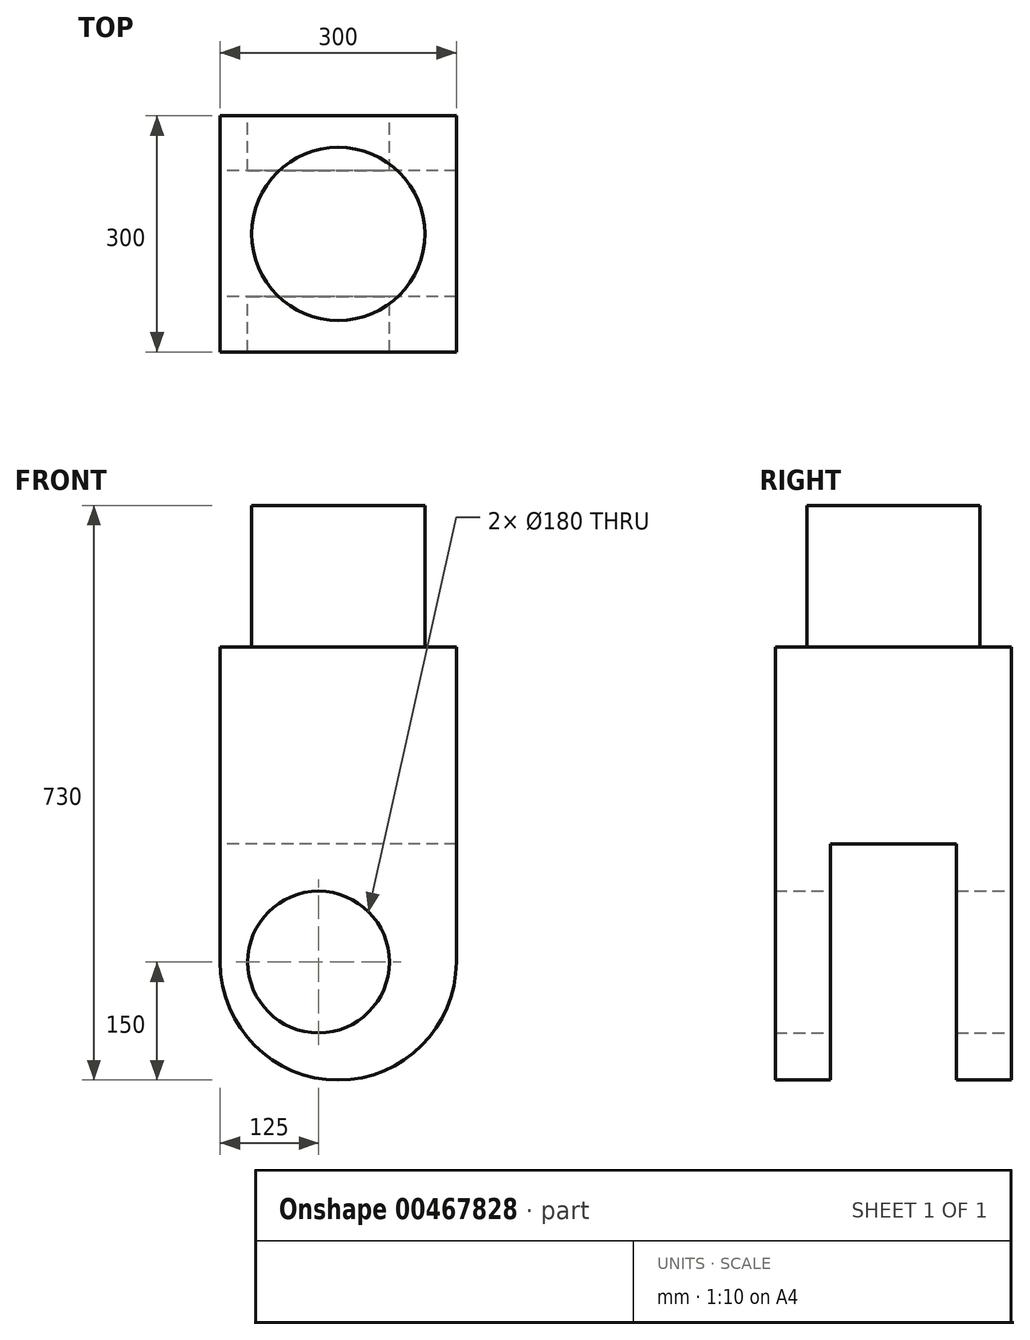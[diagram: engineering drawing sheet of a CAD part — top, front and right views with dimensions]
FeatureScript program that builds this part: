
annotation { "Feature Type Name" : "Feature", "Feature Type Description" : "" }
export const myFeature = defineFeature(function(context is Context, id is Id, definition is map)
    precondition{}
    {
        {
            var Q0;
            Q0=qCreatedBy(makeId("Top.planeOp"),FACE);
            var sketch = newSketch(context, id + "F0", { "sketchPlane" : qUnion([Q0])});
            skCircle(sketch, "E0", {"center": v(0, 0) * mm, "radius": 90 * mm});
            skSolve(sketch);
        }
        {
            var Q0;
            Q0 = qSketchRegion(id + "F0", true);
            extrude(context, id + "F1", {"entities" : qUnion([Q0]), "depth" : 180 * mm});
        }
        {
            var Q0;
            Q0=makeQuery(id+"F1.opExtrude","CAP_FACE",FACE,{"disambiguationData":[OSD([sQuery(id+"F0.wireOp",EDGE,"E0")])],"isStart":true});
            var sketch = newSketch(context, id + "F2", { "sketchPlane" : qUnion([Q0])});
            skLineSegment(sketch, "E1.bottom", {"start": v(150, 150) * mm, "end": v(-150, 150) * mm});
            skLineSegment(sketch, "E1.top", {"start": v(150, -150) * mm, "end": v(-150, -150) * mm});
            skLineSegment(sketch, "E1.left", {"start": v(150, 150) * mm, "end": v(150, -150) * mm});
            skLineSegment(sketch, "E1.right", {"start": v(-150, 150) * mm, "end": v(-150, -150) * mm});
            skPoint(sketch, "E1.middle", {"position": v(0, 0) * mm});
            skSolve(sketch);
        }
        {
            var Q0;
            Q0 = qSketchRegion(id + "F2", true);
            extrude(context, id + "F3", {"entities" : qUnion([Q0]), "operationType" : NewBodyOperationType.ADD, "depth" : 400 * mm, "offsetDistance" : 25 * mm});
        }
        {
            var Q0;
            Q0=makeQuery(id+"F3.opExtrude","SWEPT_FACE",FACE,{"disambiguationData":[OSD([sQuery(id+"F2.wireOp",EDGE,"E1.top")])]});
            var sketch = newSketch(context, id + "F4", { "sketchPlane" : qUnion([Q0])});
            skArc(sketch, "E2", {"start": v(-150, -400) * mm, "mid": v(0, -550) * mm, "end": v(150, -400) * mm});
            skLineSegment(sketch, "E3", {"start": v(150, -400) * mm, "end": v(-150, -400) * mm});
            skSolve(sketch);
        }
        {
            var Q0;
            Q0 = qSketchRegion(id + "F4", true);
            extrude(context, id + "F5", {"entities" : qUnion([Q0]), "operationType" : NewBodyOperationType.ADD, "oppositeDirection" : true, "depth" : 300 * mm});
        }
        {
            var Q0;
            Q0=makeQuery(id+"F5.boolean.opBoolean","MERGE",FACE,{"derivedFrom":[makeQuery(id+"F3.opExtrude","SWEPT_FACE",FACE,{"disambiguationData":[OSD([sQuery(id+"F2.wireOp",EDGE,"E1.top")])]}),makeQuery(id+"F5.opExtrude","CAP_FACE",FACE,{"disambiguationData":[OSD([sQuery(id+"F4.wireOp",EDGE,"E2"),sQuery(id+"F4.wireOp",EDGE,"E3")])],"isStart":true})]});
            var sketch = newSketch(context, id + "F6", { "sketchPlane" : qUnion([Q0])});
            skCircle(sketch, "E4", {"center": v(25, -400) * mm, "radius": 90 * mm});
            skSolve(sketch);
        }
        {
            var Q0;
            Q0 = qSketchRegion(id + "F6", true);
            extrude(context, id + "F7", {"entities" : qUnion([Q0]), "operationType" : NewBodyOperationType.REMOVE, "oppositeDirection" : true, "depth" : 300 * mm});
        }
        {
            var Q0;
            Q0=makeQuery(id+"F3.opExtrude","SWEPT_FACE",FACE,{"disambiguationData":[OSD([sQuery(id+"F2.wireOp",EDGE,"E1.right")])]});
            var sketch = newSketch(context, id + "F8", { "sketchPlane" : qUnion([Q0])});
            skLineSegment(sketch, "E5.bottom", {"start": v(-80, -250) * mm, "end": v(80, -250) * mm});
            skLineSegment(sketch, "E5.top", {"start": v(-80, -550) * mm, "end": v(80, -550) * mm});
            skLineSegment(sketch, "E5.left", {"start": v(-80, -250) * mm, "end": v(-80, -550) * mm});
            skLineSegment(sketch, "E5.right", {"start": v(80, -250) * mm, "end": v(80, -550) * mm});
            skPoint(sketch, "E5.middle", {"position": v(0, -400) * mm});
            skSolve(sketch);
        }
        {
            var Q0;
            Q0 = qSketchRegion(id + "F8", true);
            extrude(context, id + "F9", {"entities" : qUnion([Q0]), "operationType" : NewBodyOperationType.REMOVE, "oppositeDirection" : true, "depth" : 303 * mm});
        }
        {
            var Q0;
            Q0=makeQuery(id+"F1.opExtrude","CAP_FACE",FACE,{"disambiguationData":[OSD([sQuery(id+"F0.wireOp",EDGE,"E0")])],"isStart":false});
            var sketch = newSketch(context, id + "F10", { "sketchPlane" : qUnion([Q0])});
            skCircle(sketch, "E6", {"center": v(0, 0) * mm, "radius": 110 * mm});
            skSolve(sketch);
        }
        {
            var Q0;
            Q0 = qSketchRegion(id + "F10", true);
            extrude(context, id + "F11", {"entities" : qUnion([Q0]), "operationType" : NewBodyOperationType.ADD, "oppositeDirection" : true, "depth" : 211 * mm});
        }
    });
